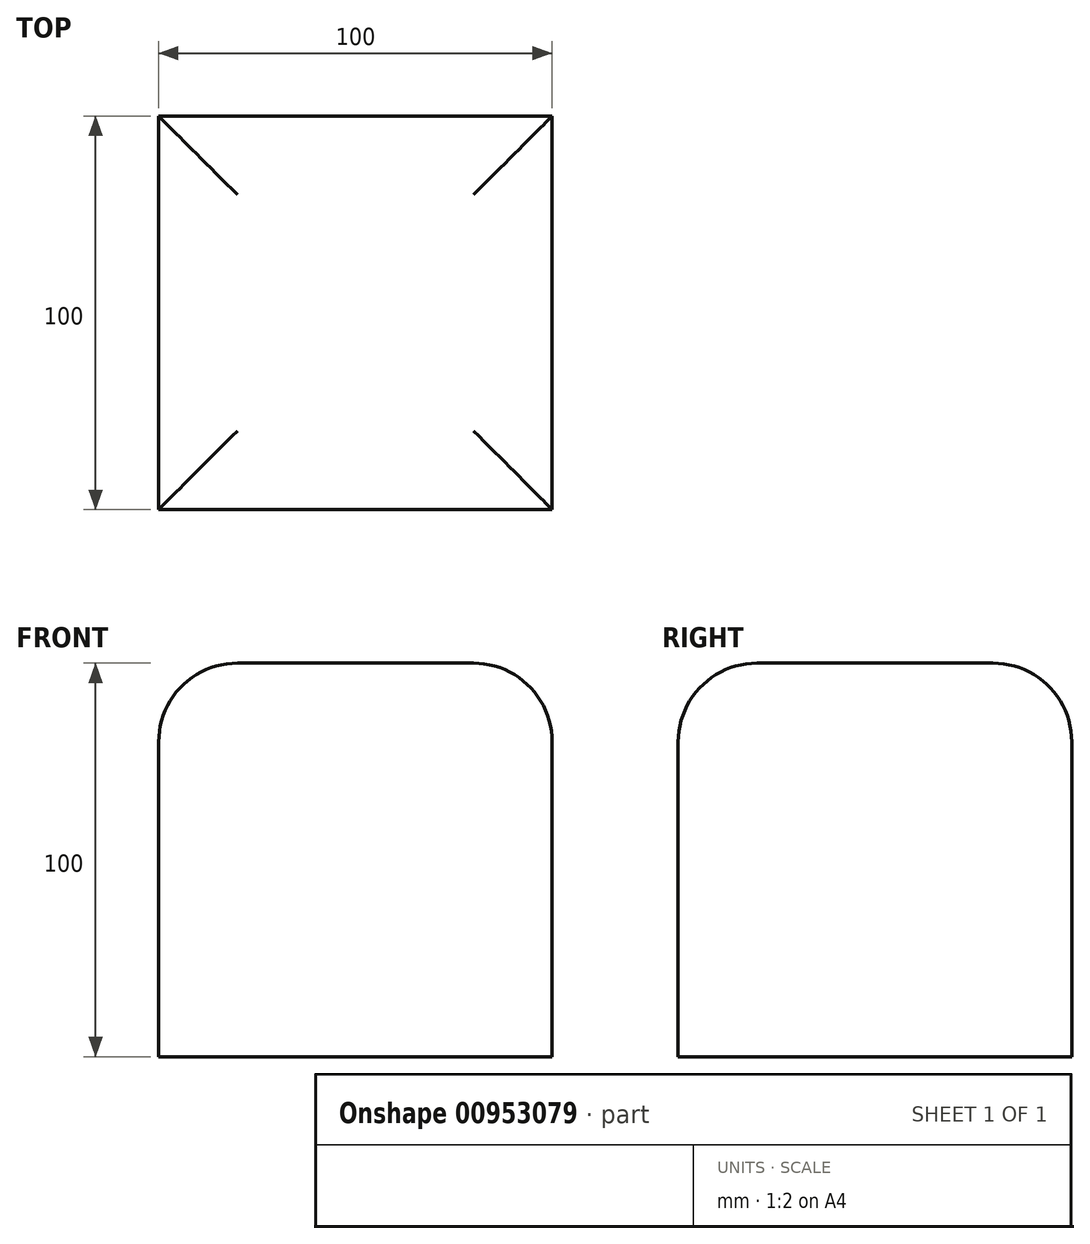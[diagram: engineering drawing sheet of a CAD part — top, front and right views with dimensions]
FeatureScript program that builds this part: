
annotation { "Feature Type Name" : "Feature", "Feature Type Description" : "" }
export const myFeature = defineFeature(function(context is Context, id is Id, definition is map)
    precondition{}
    {
        {
            var Q0;
            Q0=qCreatedBy(makeId("Top.planeOp"),FACE);
            var sketch = newSketch(context, id + "F0", { "sketchPlane" : qUnion([Q0])});
            skLineSegment(sketch, "E0.bottom", {"start": v(0, 0) * mm, "end": v(100, 0) * mm});
            skLineSegment(sketch, "E0.top", {"start": v(0, -100) * mm, "end": v(100, -100) * mm});
            skLineSegment(sketch, "E0.left", {"start": v(0, 0) * mm, "end": v(0, -100) * mm});
            skLineSegment(sketch, "E0.right", {"start": v(100, 0) * mm, "end": v(100, -100) * mm});
            skSolve(sketch);
        }
        {
            var Q0;
            Q0 = qSketchRegion(id + "F0", true);
            extrude(context, id + "F1", {"entities" : qUnion([Q0]), "depth" : 100 * mm, "offsetDistance" : 25 * mm});
        }
        {
            var Q0;
            Q0=makeQuery(id+"F1.opExtrude","CAP_EDGE",EDGE,{"disambiguationData":[OSD([sQuery(id+"F0.wireOp",EDGE,"E0.top")])],"isStart":false});
            var Q1;
            Q1=makeQuery(id+"F1.opExtrude","CAP_EDGE",EDGE,{"disambiguationData":[OSD([sQuery(id+"F0.wireOp",EDGE,"E0.right")])],"isStart":false});
            var Q2;
            Q2=makeQuery(id+"F1.opExtrude","CAP_EDGE",EDGE,{"disambiguationData":[OSD([sQuery(id+"F0.wireOp",EDGE,"E0.bottom")])],"isStart":false});
            var Q3;
            Q3=makeQuery(id+"F1.opExtrude","CAP_EDGE",EDGE,{"disambiguationData":[OSD([sQuery(id+"F0.wireOp",EDGE,"E0.left")])],"isStart":false});
            fillet(context, id + "F2", {"entities" : qUnion([Q0, Q1, Q2, Q3]), "tangentPropagation" : true, "radius" : 20 * mm, "defaultsChanged" : true, "vertexSettings" : [], "allowEdgeOverflow" : false});
        }
    });
